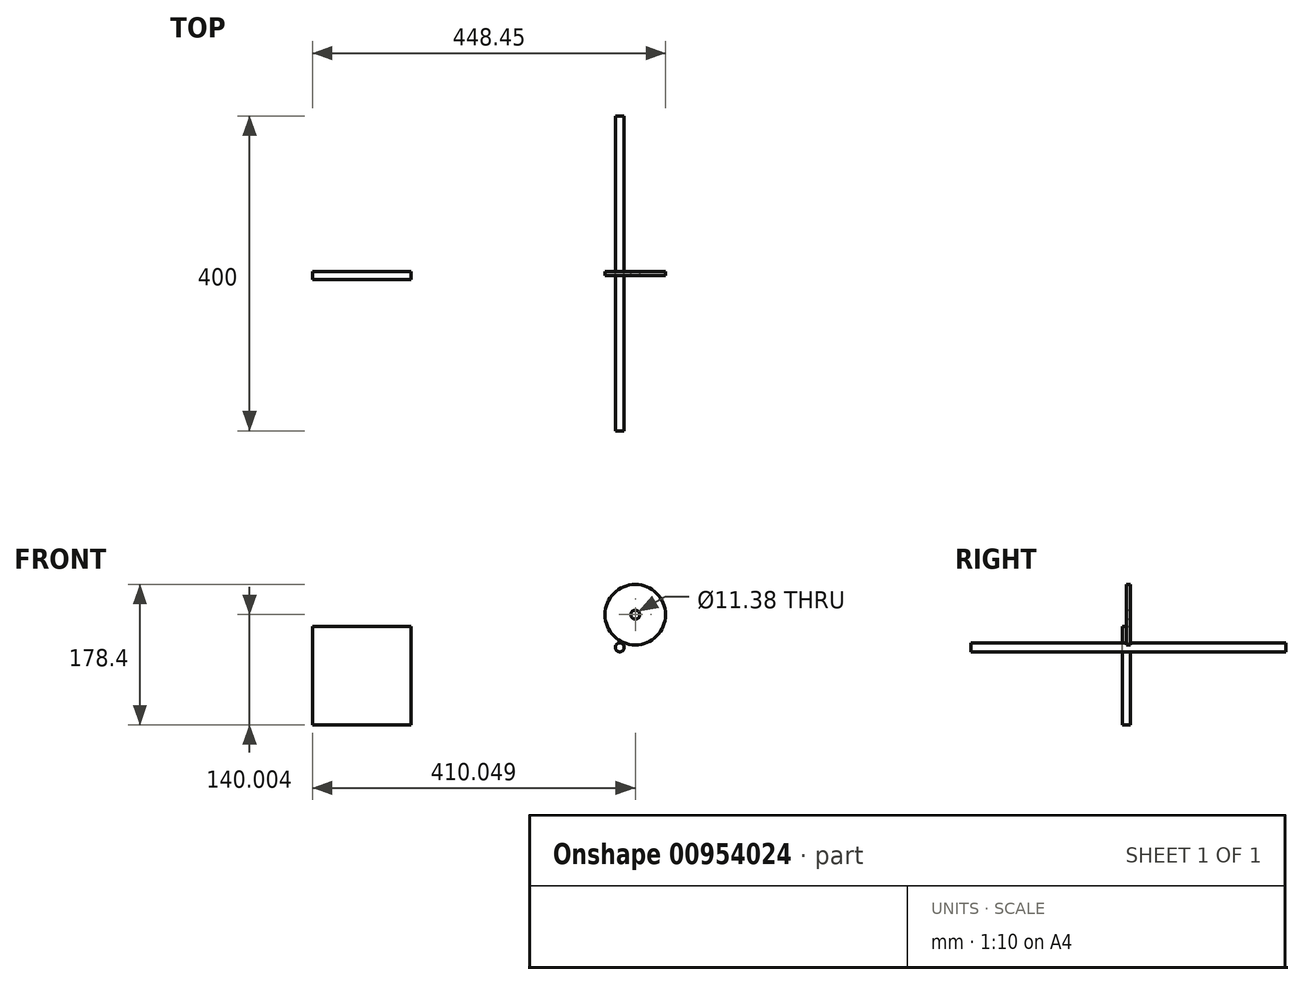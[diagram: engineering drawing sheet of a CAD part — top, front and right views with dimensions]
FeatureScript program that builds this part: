
annotation { "Feature Type Name" : "Feature", "Feature Type Description" : "" }
export const myFeature = defineFeature(function(context is Context, id is Id, definition is map)
    precondition{}
    {
        {
            var Q0;
            Q0=qCreatedBy(makeId("Front.planeOp"),FACE);
            var sketch = newSketch(context, id + "F0", { "sketchPlane" : qUnion([Q0])});
            skCircle(sketch, "E0", {"center": v(0, 0) * mm, "radius": 5.68 * mm});
            skLineSegment(sketch, "E1", {"start": v(0, 5.68) * mm, "end": v(0, -5.68) * mm});
            skCircle(sketch, "E2", {"center": v(19.73, 41.61) * mm, "radius": 5.69 * mm});
            skLineSegment(sketch, "E3.bottom", {"start": v(-265.32, -98.39) * mm, "end": v(-390.32, -98.39) * mm});
            skLineSegment(sketch, "E3.top", {"start": v(-265.32, 26.61) * mm, "end": v(-390.32, 26.61) * mm});
            skLineSegment(sketch, "E3.left", {"start": v(-265.32, -98.39) * mm, "end": v(-265.32, 26.61) * mm});
            skLineSegment(sketch, "E3.right", {"start": v(-390.32, -98.39) * mm, "end": v(-390.32, 26.61) * mm});
            skPoint(sketch, "E3.middle", {"position": v(-327.82, -35.89) * mm});
            skCircle(sketch, "E4", {"center": v(19.73, 41.61) * mm, "radius": 38.4 * mm});
            skSolve(sketch);
        }
        {
            var Q0;
            Q0=makeQuery(id+"F0.imprint","IMPRINT",FACE,{"disambiguationData":[TD([[makeQuery(id+"F0.imprint","IMPRINT",EDGE,{"derivedFrom":sQuery(id+"F0.wireOp",EDGE,"E0")}),1.0]])]});
            extrude(context, id + "F1", {"entities" : qUnion([Q0]), "endBound" : BoundingType.SYMMETRIC, "depth" : 400 * mm, "offsetDistance" : 25.4 * mm});
        }
        {
            var Q0;
            Q0 = qSketchRegion(id + "F0", true);
            extrude(context, id + "F2", {"entities" : qUnion([Q0]), "operationType" : NewBodyOperationType.ADD, "endBound" : BoundingType.SYMMETRIC, "depth" : 5 * mm, "offsetDistance" : 25.4 * mm});
        }
        {
            var Q0;
            Q0=makeQuery(id+"F2.opExtrude","CAP_FACE",FACE,{"disambiguationData":[OSD([sQuery(id+"F0.wireOp",EDGE,"E3.bottom"),sQuery(id+"F0.wireOp",EDGE,"E3.top"),sQuery(id+"F0.wireOp",EDGE,"E3.left"),sQuery(id+"F0.wireOp",EDGE,"E3.right")])],"isStart":false});
            extrude(context, id + "F3", {"entities" : qUnion([Q0]), "operationType" : NewBodyOperationType.ADD, "depth" : 5 * mm, "offsetDistance" : 25.4 * mm});
        }
    });
